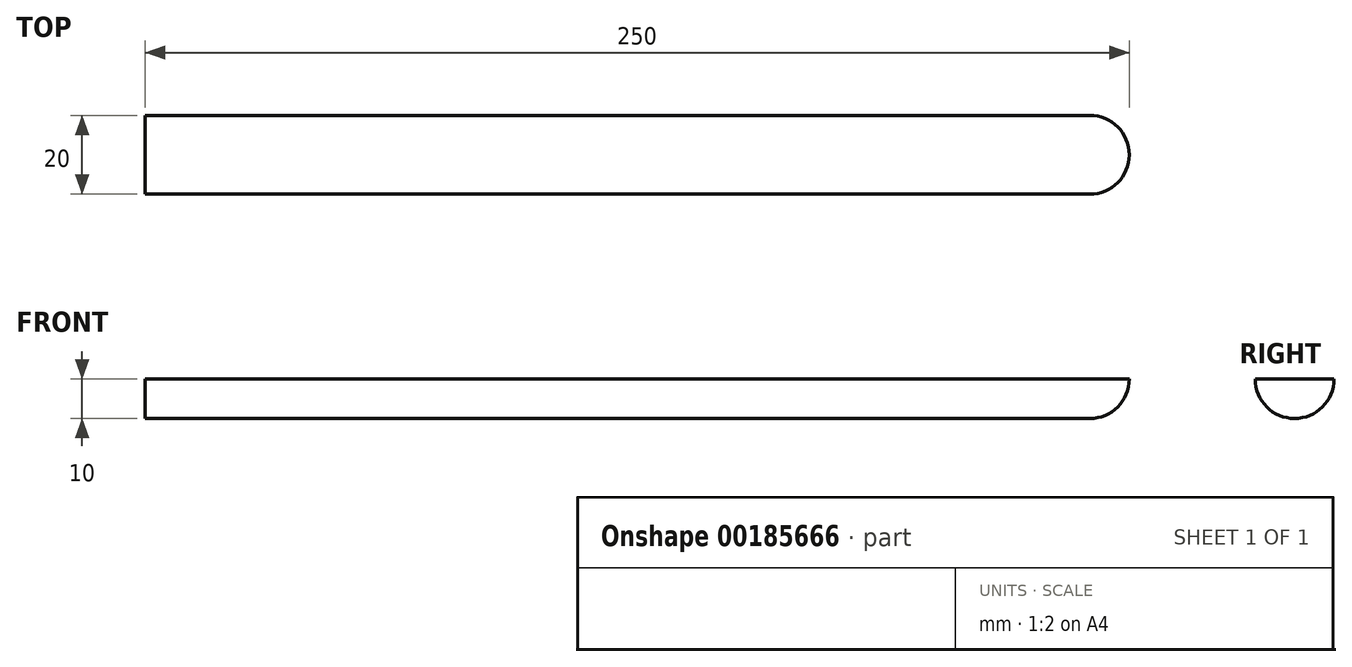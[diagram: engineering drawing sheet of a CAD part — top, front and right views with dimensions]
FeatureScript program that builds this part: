
annotation { "Feature Type Name" : "Feature", "Feature Type Description" : "" }
export const myFeature = defineFeature(function(context is Context, id is Id, definition is map)
    precondition{}
    {
        {
            var Q0;
            Q0=qCreatedBy(makeId("Top.planeOp"),FACE);
            var sketch = newSketch(context, id + "F0", { "sketchPlane" : qUnion([Q0])});
            skLineSegment(sketch, "E0.bottom", {"start": v(125, 10) * mm, "end": v(-125, 10) * mm});
            skLineSegment(sketch, "E0.top", {"start": v(125, -10) * mm, "end": v(-125, -10) * mm});
            skLineSegment(sketch, "E0.left", {"start": v(125, 10) * mm, "end": v(125, -10) * mm});
            skLineSegment(sketch, "E0.right", {"start": v(-125, 10) * mm, "end": v(-125, -10) * mm});
            skPoint(sketch, "E0.middle", {"position": v(0, 0) * mm});
            skLineSegment(sketch, "E1", {"start": v(-125, 0) * mm, "end": v(125, 0) * mm});
            skSolve(sketch);
        }
        {
            var Q0;
            {var subQ0=sQuery(id+"F0.wireOp",EDGE,"E0.top");Q0=makeQuery(id+"F0.imprint","IMPRINT",FACE,{"disambiguationData":[TD([[makeQuery(id+"F0.imprint","IMPRINT",EDGE,{"derivedFrom":subQ0}),-1.0]])]});}
            var Q1;
            Q1=sQuery(id+"F0.wireOp",EDGE,"E1");
            revolve(context, id + "F1", {"entities" : qUnion([Q0]), "axis" : qUnion([Q1]), "revolveType" : RevolveType.ONE_DIRECTION, "angle" : 180 * degree});
        }
        {
            var Q0;
            Q0=makeQuery(id+"F1.opRevolve","SWEPT_EDGE",EDGE,{"disambiguationData":[OSD([sQuery(id+"F0.wireOp",EDGE,"E0.top"),sQuery(id+"F0.wireOp",EDGE,"E0.left")])]});
            fillet(context, id + "F2", {"entities" : qUnion([Q0]), "radius" : 10 * mm, "tangentPropagation" : true, "allowEdgeOverflow" : false});
        }
    });
